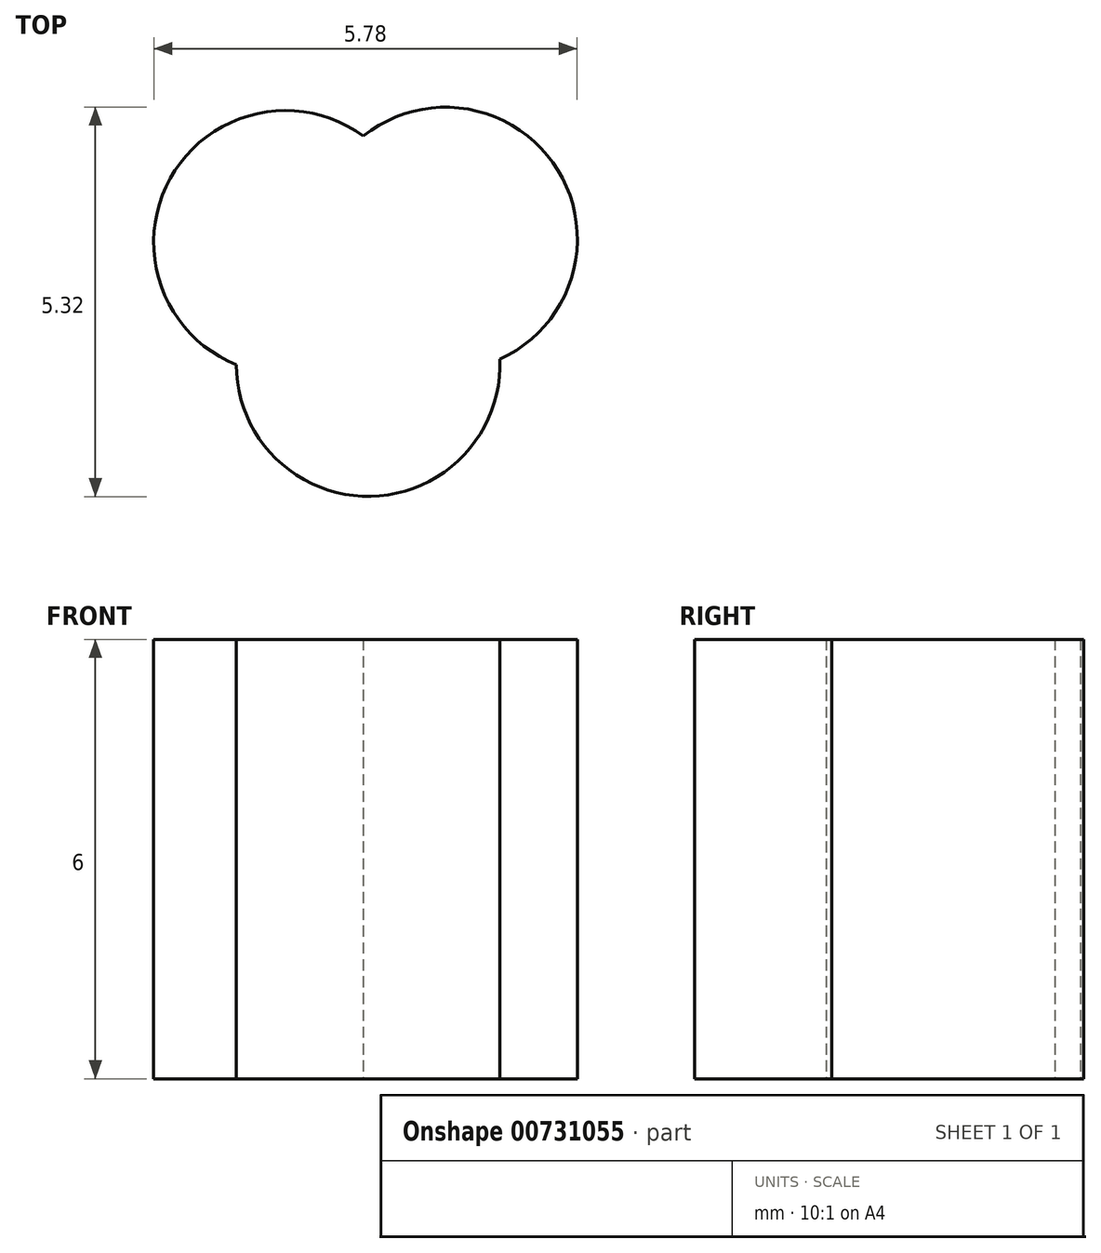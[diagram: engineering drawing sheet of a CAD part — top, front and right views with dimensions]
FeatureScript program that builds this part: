
annotation { "Feature Type Name" : "Feature", "Feature Type Description" : "" }
export const myFeature = defineFeature(function(context is Context, id is Id, definition is map)
    precondition{}
    {
        {
            var Q0;
            Q0=qCreatedBy(makeId("Top.planeOp"),FACE);
            var sketch = newSketch(context, id + "F0", { "sketchPlane" : qUnion([Q0])});
            skCircle(sketch, "E0", {"center": v(-786.71, 315.48) * mm, "radius": 1.8 * mm});
            skCircle(sketch, "E1", {"center": v(-784.53, 315.53) * mm, "radius": 1.8 * mm});
            skCircle(sketch, "E2", {"center": v(-785.62, 315) * mm, "radius": 3 * mm});
            skCircle(sketch, "E3", {"center": v(-785.58, 313.81) * mm, "radius": 1.8 * mm});
            skSolve(sketch);
        }
        {
            var Q0;
            {var subQ0=sQuery(id+"F0.wireOp",EDGE,"E2");var subQ1=sQuery(id+"F0.wireOp",EDGE,"E1");var subQ2=makeQuery(id+"F0.imprint","INTERSECT",VERTEX,{"disambiguationData":[OD(0.0)],"derivedFrom":[subQ1,subQ0]});Q0=makeQuery(id+"F0.imprint","IMPRINT",FACE,{"disambiguationData":[TD([[makeQuery(id+"F0.imprint","IMPRINT",EDGE,{"disambiguationData":[TD([[subQ2,1.0]])],"derivedFrom":subQ1}),1.0]])]});}
            var Q1;
            {var subQ0=sQuery(id+"F0.wireOp",EDGE,"E3");var subQ1=sQuery(id+"F0.wireOp",EDGE,"E0");var subQ2=makeQuery(id+"F0.imprint","INTERSECT",VERTEX,{"disambiguationData":[OD(1.0)],"derivedFrom":[subQ1,subQ0]});Q1=makeQuery(id+"F0.imprint","IMPRINT",FACE,{"disambiguationData":[TD([[makeQuery(id+"F0.imprint","IMPRINT",EDGE,{"disambiguationData":[TD([[subQ2,-1.0]])],"derivedFrom":subQ1}),-1.0]])]});}
            var Q2;
            {var subQ0=sQuery(id+"F0.wireOp",EDGE,"E3");var subQ1=sQuery(id+"F0.wireOp",EDGE,"E0");var subQ2=makeQuery(id+"F0.imprint","INTERSECT",VERTEX,{"disambiguationData":[OD(1.0)],"derivedFrom":[subQ1,subQ0]});Q2=makeQuery(id+"F0.imprint","IMPRINT",FACE,{"disambiguationData":[TD([[makeQuery(id+"F0.imprint","IMPRINT",EDGE,{"disambiguationData":[TD([[subQ2,-1.0]])],"derivedFrom":subQ1}),1.0]])]});}
            var Q3;
            {var subQ0=sQuery(id+"F0.wireOp",EDGE,"E1");var subQ1=sQuery(id+"F0.wireOp",EDGE,"E0");var subQ2=makeQuery(id+"F0.imprint","INTERSECT",VERTEX,{"disambiguationData":[OD(0.0)],"derivedFrom":[subQ1,subQ0]});Q3=makeQuery(id+"F0.imprint","IMPRINT",FACE,{"disambiguationData":[TD([[makeQuery(id+"F0.imprint","IMPRINT",EDGE,{"disambiguationData":[TD([[subQ2,-1.0]])],"derivedFrom":subQ1}),1.0]])]});}
            var Q4;
            {var subQ1=sQuery(id+"F0.wireOp",EDGE,"E1");var subQ6=sQuery(id+"F0.wireOp",EDGE,"E0");var subQ7=makeQuery(id+"F0.imprint","INTERSECT",VERTEX,{"disambiguationData":[OD(0.0)],"derivedFrom":[subQ6,subQ1]});Q4=makeQuery(id+"F0.imprint","IMPRINT",FACE,{"disambiguationData":[TD([[makeQuery(id+"F0.imprint","IMPRINT",EDGE,{"disambiguationData":[TD([[subQ7,1.0]])],"derivedFrom":subQ6}),-1.0]])]});}
            var Q5;
            {var subQ0=sQuery(id+"F0.wireOp",EDGE,"E3");var subQ1=sQuery(id+"F0.wireOp",EDGE,"E0");var subQ2=makeQuery(id+"F0.imprint","INTERSECT",VERTEX,{"disambiguationData":[OD(0.0)],"derivedFrom":[subQ1,subQ0]});Q5=makeQuery(id+"F0.imprint","IMPRINT",FACE,{"disambiguationData":[TD([[makeQuery(id+"F0.imprint","IMPRINT",EDGE,{"disambiguationData":[TD([[subQ2,1.0]])],"derivedFrom":subQ1}),-1.0]])]});}
            var Q6;
            {var subQ0=sQuery(id+"F0.wireOp",EDGE,"E3");var subQ1=sQuery(id+"F0.wireOp",EDGE,"E0");var subQ2=makeQuery(id+"F0.imprint","INTERSECT",VERTEX,{"disambiguationData":[OD(0.0)],"derivedFrom":[subQ1,subQ0]});Q6=makeQuery(id+"F0.imprint","IMPRINT",FACE,{"disambiguationData":[TD([[makeQuery(id+"F0.imprint","IMPRINT",EDGE,{"disambiguationData":[TD([[subQ2,1.0]])],"derivedFrom":subQ1}),1.0]])]});}
            var Q7;
            {var subQ0=sQuery(id+"F0.wireOp",EDGE,"E1");var subQ1=sQuery(id+"F0.wireOp",EDGE,"E0");var subQ2=makeQuery(id+"F0.imprint","INTERSECT",VERTEX,{"disambiguationData":[OD(0.0)],"derivedFrom":[subQ1,subQ0]});Q7=makeQuery(id+"F0.imprint","IMPRINT",FACE,{"disambiguationData":[TD([[makeQuery(id+"F0.imprint","IMPRINT",EDGE,{"disambiguationData":[TD([[subQ2,1.0]])],"derivedFrom":subQ1}),1.0]])]});}
            extrude(context, id + "F1", {"entities" : qUnion([Q0, Q1, Q2, Q3, Q4, Q5, Q6, Q7]), "depth" : 6 * mm, "offsetDistance" : 25.4 * mm});
        }
    });
